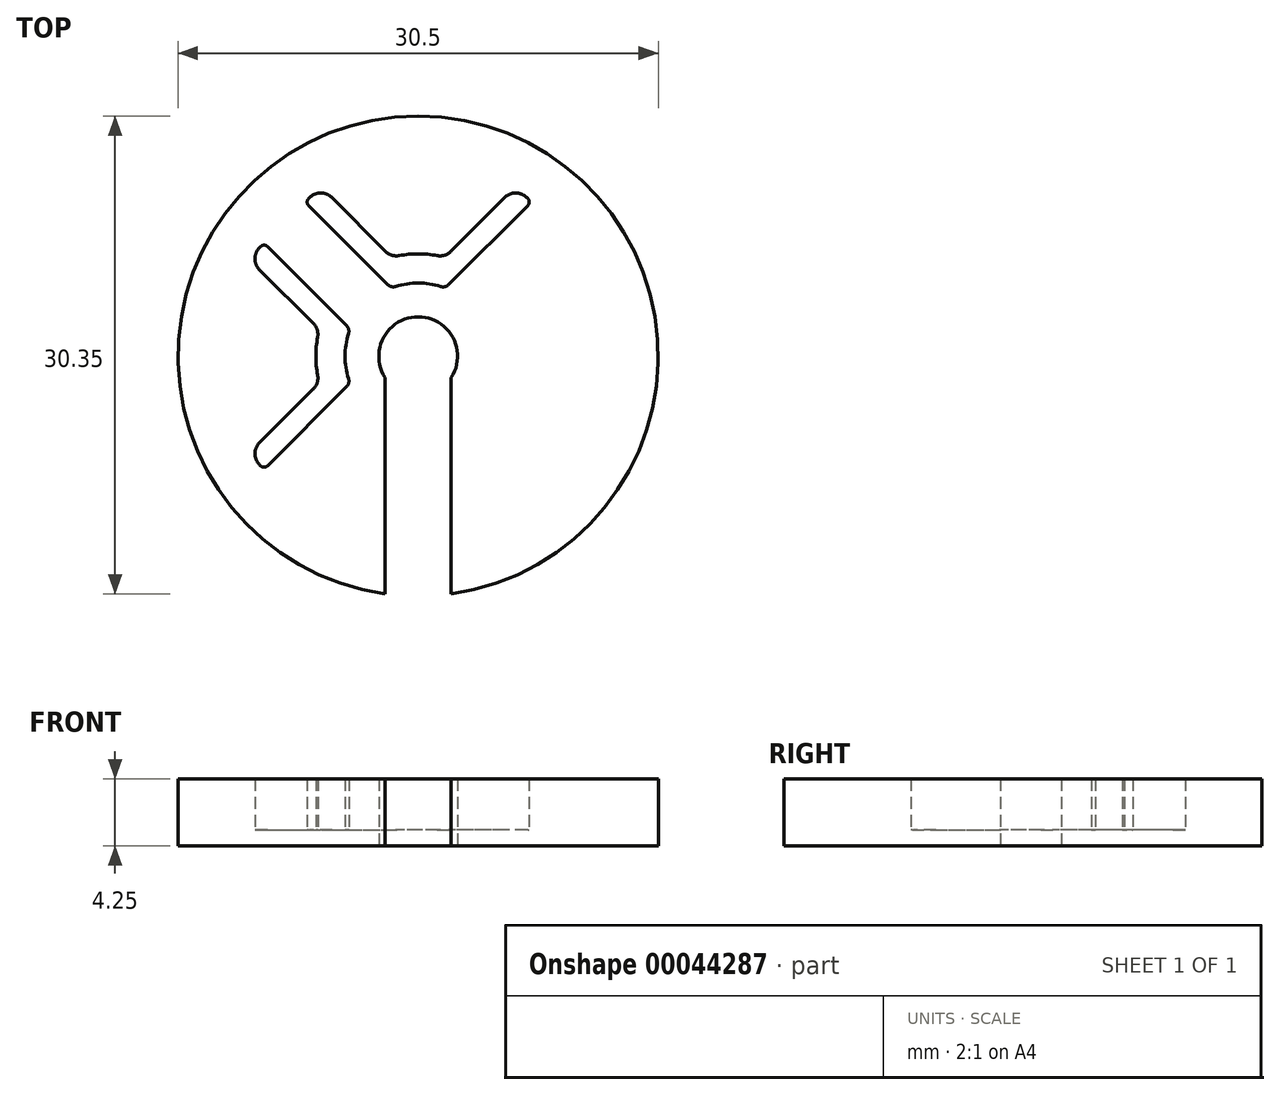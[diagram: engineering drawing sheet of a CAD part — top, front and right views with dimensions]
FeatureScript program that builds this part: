
annotation { "Feature Type Name" : "Feature", "Feature Type Description" : "" }
export const myFeature = defineFeature(function(context is Context, id is Id, definition is map)
    precondition{}
    {
        {
            var Q0;
            Q0=qCreatedBy(makeId("Top.planeOp"),FACE);
            var sketch = newSketch(context, id + "F0", { "sketchPlane" : qUnion([Q0])});
            skCircle(sketch, "E0", {"center": v(0, 0) * mm, "radius": 15.25 * mm});
            skSolve(sketch);
        }
        {
            var Q0;
            Q0 = qSketchRegion(id + "F0", true);
            extrude(context, id + "F1", {"entities" : qUnion([Q0]), "oppositeDirection" : true, "depth" : 1 * mm});
        }
        {
            var Q0;
            Q0=qCreatedBy(makeId("Top.planeOp"),FACE);
            var sketch = newSketch(context, id + "F2", { "sketchPlane" : qUnion([Q0])});
            skLineSegment(sketch, "E1", {"start": v(0, 0) * mm, "end": v(8.49, 8.49) * mm});
            skLineSegment(sketch, "E2", {"start": v(10, 6.97) * mm, "end": v(10.07, 6.9) * mm});
            skArc(sketch, "E3", {"start": v(4.65, 0) * mm, "mid": v(4.6, 0.72) * mm, "end": v(4.43, 1.43) * mm});
            skArc(sketch, "E4.MirrorC", {"start": v(6.39, 1.2) * mm, "mid": v(6.47, 0.6) * mm, "end": v(6.5, 0) * mm});
            skLineSegment(sketch, "E5", {"start": v(9.58, 6.97) * mm, "end": v(4.55, 1.93) * mm});
            skLineSegment(sketch, "E6", {"start": v(10.07, 5.48) * mm, "end": v(6.67, 2.1) * mm});
            skPoint(sketch, "E7.visualSharp", {"position": v(4.32, 1.7) * mm});
            skArc(sketch, "E7.filletArc", {"start": v(4.55, 1.93) * mm, "mid": v(4.42, 1.7) * mm, "end": v(4.43, 1.43) * mm});
            skPoint(sketch, "E8.visualSharp", {"position": v(6.27, 1.7) * mm});
            skArc(sketch, "E8.filletArc", {"start": v(6.67, 2.1) * mm, "mid": v(6.42, 1.69) * mm, "end": v(6.39, 1.2) * mm});
            skPoint(sketch, "E9.visualSharp", {"position": v(9.8, 7.18) * mm});
            skArc(sketch, "E9.filletArc", {"start": v(10, 6.97) * mm, "mid": v(9.8, 7.05) * mm, "end": v(9.58, 6.97) * mm});
            skPoint(sketch, "E10.visualSharp", {"position": v(10.78, 6.19) * mm});
            skArc(sketch, "E10.filletArc", {"start": v(10.07, 5.48) * mm, "mid": v(10.37, 6.19) * mm, "end": v(10.07, 6.9) * mm});
            skArc(sketch, "E11.MirrorCS", {"start": v(1.93, 4.55) * mm, "mid": v(1.7, 4.42) * mm, "end": v(1.43, 4.43) * mm});
            skArc(sketch, "E12.MirrorCS", {"start": v(6.97, 10) * mm, "mid": v(7.05, 9.8) * mm, "end": v(6.97, 9.58) * mm});
            skLineSegment(sketch, "E13.MirrorCS", {"start": v(6.97, 10) * mm, "end": v(6.9, 10.07) * mm});
            skArc(sketch, "E14.MirrorCS", {"start": v(2.1, 6.67) * mm, "mid": v(1.69, 6.42) * mm, "end": v(1.2, 6.39) * mm});
            skArc(sketch, "E15.MirrorCS", {"start": v(5.48, 10.07) * mm, "mid": v(6.19, 10.37) * mm, "end": v(6.9, 10.07) * mm});
            skLineSegment(sketch, "E16.MirrorCS", {"start": v(5.48, 10.07) * mm, "end": v(2.1, 6.67) * mm});
            skPoint(sketch, "E17.MirrorP", {"position": v(7.18, 9.8) * mm});
            skPoint(sketch, "E18.MirrorP", {"position": v(1.7, 4.32) * mm});
            skPoint(sketch, "E19.MirrorP", {"position": v(6.19, 10.78) * mm});
            skLineSegment(sketch, "E20.MirrorCS", {"start": v(6.97, 9.58) * mm, "end": v(1.93, 4.55) * mm});
            skArc(sketch, "E21.MirrorCS", {"start": v(1.2, 6.39) * mm, "mid": v(0.6, 6.47) * mm, "end": v(0, 6.5) * mm});
            skArc(sketch, "E22.MirrorCS", {"start": v(0, 4.65) * mm, "mid": v(0.72, 4.6) * mm, "end": v(1.43, 4.43) * mm});
            skPoint(sketch, "E23.MirrorP", {"position": v(1.7, 6.27) * mm});
            skArc(sketch, "E24.MirrorCS", {"start": v(-6.97, 10) * mm, "mid": v(-7.05, 9.8) * mm, "end": v(-6.97, 9.58) * mm});
            skArc(sketch, "E25.MirrorCS", {"start": v(-10, 6.97) * mm, "mid": v(-9.8, 7.05) * mm, "end": v(-9.58, 6.97) * mm});
            skArc(sketch, "E26.MirrorCS", {"start": v(-1.93, 4.55) * mm, "mid": v(-1.7, 4.42) * mm, "end": v(-1.43, 4.43) * mm});
            skLineSegment(sketch, "E27.MirrorCS", {"start": v(-6.97, 10) * mm, "end": v(-6.9, 10.07) * mm});
            skLineSegment(sketch, "E28.MirrorCS", {"start": v(-10, 6.97) * mm, "end": v(-10.07, 6.9) * mm});
            skArc(sketch, "E29.MirrorCS", {"start": v(-4.55, 1.93) * mm, "mid": v(-4.42, 1.7) * mm, "end": v(-4.43, 1.43) * mm});
            skArc(sketch, "E30.MirrorCS", {"start": v(-6.67, 2.1) * mm, "mid": v(-6.42, 1.69) * mm, "end": v(-6.39, 1.2) * mm});
            skArc(sketch, "E31.MirrorCS", {"start": v(-2.1, 6.67) * mm, "mid": v(-1.69, 6.42) * mm, "end": v(-1.2, 6.39) * mm});
            skArc(sketch, "E32.MirrorCS", {"start": v(-10.07, 5.48) * mm, "mid": v(-10.37, 6.19) * mm, "end": v(-10.07, 6.9) * mm});
            skArc(sketch, "E33.MirrorCS", {"start": v(-6.39, 1.2) * mm, "mid": v(-6.47, 0.6) * mm, "end": v(-6.5, 0) * mm});
            skArc(sketch, "E34.MirrorCS", {"start": v(-4.65, 0) * mm, "mid": v(-4.6, 0.72) * mm, "end": v(-4.43, 1.43) * mm});
            skArc(sketch, "E35.MirrorCS", {"start": v(-1.2, 6.39) * mm, "mid": v(-0.6, 6.47) * mm, "end": v(0, 6.5) * mm});
            skArc(sketch, "E36.MirrorCS", {"start": v(-5.48, 10.07) * mm, "mid": v(-6.19, 10.37) * mm, "end": v(-6.9, 10.07) * mm});
            skLineSegment(sketch, "E37.MirrorCS", {"start": v(-6.97, 9.58) * mm, "end": v(-1.93, 4.55) * mm});
            skLineSegment(sketch, "E38.MirrorCS", {"start": v(-5.48, 10.07) * mm, "end": v(-2.1, 6.67) * mm});
            skPoint(sketch, "E39.MirrorP", {"position": v(-9.8, 7.18) * mm});
            skPoint(sketch, "E40.MirrorP", {"position": v(-1.7, 6.27) * mm});
            skPoint(sketch, "E41.MirrorP", {"position": v(-7.18, 9.8) * mm});
            skArc(sketch, "E42.MirrorCS", {"start": v(0, 4.65) * mm, "mid": v(-0.72, 4.6) * mm, "end": v(-1.43, 4.43) * mm});
            skPoint(sketch, "E43.MirrorP", {"position": v(-6.27, 1.7) * mm});
            skPoint(sketch, "E44.MirrorP", {"position": v(-1.7, 4.32) * mm});
            skPoint(sketch, "E45.MirrorP", {"position": v(-10.78, 6.19) * mm});
            skLineSegment(sketch, "E46.MirrorCS", {"start": v(0, 0) * mm, "end": v(-8.49, 8.49) * mm});
            skPoint(sketch, "E47.MirrorP", {"position": v(-4.32, 1.7) * mm});
            skLineSegment(sketch, "E48.MirrorCS", {"start": v(-10.07, 5.48) * mm, "end": v(-6.67, 2.1) * mm});
            skPoint(sketch, "E49.MirrorP", {"position": v(-6.19, 10.78) * mm});
            skLineSegment(sketch, "E50.MirrorCS", {"start": v(-9.58, 6.97) * mm, "end": v(-4.55, 1.93) * mm});
            skLineSegment(sketch, "E51.MirrorCS", {"start": v(-6.97, -10) * mm, "end": v(-6.9, -10.07) * mm});
            skLineSegment(sketch, "E52.MirrorCS", {"start": v(6.97, -10) * mm, "end": v(6.9, -10.07) * mm});
            skArc(sketch, "E53.MirrorCS", {"start": v(6.97, -10) * mm, "mid": v(7.05, -9.8) * mm, "end": v(6.97, -9.58) * mm});
            skArc(sketch, "E54.MirrorCS", {"start": v(1.93, -4.55) * mm, "mid": v(1.7, -4.42) * mm, "end": v(1.43, -4.43) * mm});
            skArc(sketch, "E55.MirrorCS", {"start": v(10, -6.97) * mm, "mid": v(9.8, -7.05) * mm, "end": v(9.58, -6.97) * mm});
            skArc(sketch, "E56.MirrorCS", {"start": v(4.55, -1.93) * mm, "mid": v(4.42, -1.7) * mm, "end": v(4.43, -1.43) * mm});
            skArc(sketch, "E57.MirrorCS", {"start": v(-4.55, -1.93) * mm, "mid": v(-4.42, -1.7) * mm, "end": v(-4.43, -1.43) * mm});
            skArc(sketch, "E58.MirrorCS", {"start": v(-10, -6.97) * mm, "mid": v(-9.8, -7.05) * mm, "end": v(-9.58, -6.97) * mm});
            skArc(sketch, "E59.MirrorCS", {"start": v(-6.97, -10) * mm, "mid": v(-7.05, -9.8) * mm, "end": v(-6.97, -9.58) * mm});
            skLineSegment(sketch, "E60.MirrorCS", {"start": v(-10, -6.97) * mm, "end": v(-10.07, -6.9) * mm});
            skLineSegment(sketch, "E61.MirrorCS", {"start": v(10, -6.97) * mm, "end": v(10.07, -6.9) * mm});
            skArc(sketch, "E62.MirrorCS", {"start": v(-1.93, -4.55) * mm, "mid": v(-1.7, -4.42) * mm, "end": v(-1.43, -4.43) * mm});
            skArc(sketch, "E63.MirrorCS", {"start": v(-6.67, -2.1) * mm, "mid": v(-6.42, -1.69) * mm, "end": v(-6.39, -1.2) * mm});
            skArc(sketch, "E64.MirrorCS", {"start": v(6.67, -2.1) * mm, "mid": v(6.42, -1.69) * mm, "end": v(6.39, -1.2) * mm});
            skArc(sketch, "E65.MirrorCS", {"start": v(2.1, -6.67) * mm, "mid": v(1.69, -6.42) * mm, "end": v(1.2, -6.39) * mm});
            skArc(sketch, "E66.MirrorCS", {"start": v(-2.1, -6.67) * mm, "mid": v(-1.69, -6.42) * mm, "end": v(-1.2, -6.39) * mm});
            skArc(sketch, "E67.MirrorCS", {"start": v(-1.2, -6.39) * mm, "mid": v(-0.6, -6.47) * mm, "end": v(0, -6.5) * mm});
            skArc(sketch, "E68.MirrorCS", {"start": v(-5.48, -10.07) * mm, "mid": v(-6.19, -10.37) * mm, "end": v(-6.9, -10.07) * mm});
            skArc(sketch, "E69.MirrorCS", {"start": v(10.07, -5.48) * mm, "mid": v(10.37, -6.19) * mm, "end": v(10.07, -6.9) * mm});
            skArc(sketch, "E70.MirrorCS", {"start": v(5.48, -10.07) * mm, "mid": v(6.19, -10.37) * mm, "end": v(6.9, -10.07) * mm});
            skArc(sketch, "E71.MirrorCS", {"start": v(4.65, 0) * mm, "mid": v(4.6, -0.72) * mm, "end": v(4.43, -1.43) * mm});
            skArc(sketch, "E72.MirrorCS", {"start": v(-10.07, -5.48) * mm, "mid": v(-10.37, -6.19) * mm, "end": v(-10.07, -6.9) * mm});
            skArc(sketch, "E73.MirrorCS", {"start": v(-4.65, 0) * mm, "mid": v(-4.6, -0.72) * mm, "end": v(-4.43, -1.43) * mm});
            skLineSegment(sketch, "E74.MirrorCS", {"start": v(6.97, -9.58) * mm, "end": v(1.93, -4.55) * mm});
            skPoint(sketch, "E75.MirrorP", {"position": v(-6.19, -10.78) * mm});
            skLineSegment(sketch, "E76.MirrorCS", {"start": v(-10.07, -5.48) * mm, "end": v(-6.67, -2.1) * mm});
            skArc(sketch, "E77.MirrorCS", {"start": v(0, -4.65) * mm, "mid": v(0.72, -4.6) * mm, "end": v(1.43, -4.43) * mm});
            skArc(sketch, "E78.MirrorCS", {"start": v(0, -4.65) * mm, "mid": v(-0.72, -4.6) * mm, "end": v(-1.43, -4.43) * mm});
            skPoint(sketch, "E79.MirrorP", {"position": v(-1.7, -4.32) * mm});
            skLineSegment(sketch, "E80.MirrorCS", {"start": v(10.07, -5.48) * mm, "end": v(6.67, -2.1) * mm});
            skPoint(sketch, "E81.MirrorP", {"position": v(7.18, -9.8) * mm});
            skLineSegment(sketch, "E82.MirrorCS", {"start": v(9.58, -6.97) * mm, "end": v(4.55, -1.93) * mm});
            skArc(sketch, "E83.MirrorCS", {"start": v(-6.39, -1.2) * mm, "mid": v(-6.47, -0.6) * mm, "end": v(-6.5, 0) * mm});
            skPoint(sketch, "E84.MirrorP", {"position": v(-10.78, -6.19) * mm});
            skPoint(sketch, "E85.MirrorP", {"position": v(1.7, -6.27) * mm});
            skPoint(sketch, "E86.MirrorP", {"position": v(-4.32, -1.7) * mm});
            skArc(sketch, "E87.MirrorCS", {"start": v(6.39, -1.2) * mm, "mid": v(6.47, -0.6) * mm, "end": v(6.5, 0) * mm});
            skLineSegment(sketch, "E88.MirrorCS", {"start": v(-6.97, -9.58) * mm, "end": v(-1.93, -4.55) * mm});
            skPoint(sketch, "E89.MirrorP", {"position": v(1.7, -4.32) * mm});
            skPoint(sketch, "E90.MirrorP", {"position": v(-9.8, -7.18) * mm});
            skLineSegment(sketch, "E91.MirrorCS", {"start": v(5.48, -10.07) * mm, "end": v(2.1, -6.67) * mm});
            skPoint(sketch, "E92.MirrorP", {"position": v(4.32, -1.7) * mm});
            skPoint(sketch, "E93.MirrorP", {"position": v(10.78, -6.19) * mm});
            skPoint(sketch, "E94.MirrorP", {"position": v(-6.27, -1.7) * mm});
            skArc(sketch, "E95.MirrorCS", {"start": v(1.2, -6.39) * mm, "mid": v(0.6, -6.47) * mm, "end": v(0, -6.5) * mm});
            skPoint(sketch, "E96.MirrorP", {"position": v(-7.18, -9.8) * mm});
            skPoint(sketch, "E97.MirrorP", {"position": v(6.27, -1.7) * mm});
            skLineSegment(sketch, "E98.MirrorCS", {"start": v(-5.48, -10.07) * mm, "end": v(-2.1, -6.67) * mm});
            skLineSegment(sketch, "E99.MirrorCS", {"start": v(0, 0) * mm, "end": v(-8.49, -8.49) * mm});
            skLineSegment(sketch, "E100.MirrorCS", {"start": v(-9.58, -6.97) * mm, "end": v(-4.55, -1.93) * mm});
            skLineSegment(sketch, "E101.MirrorCS", {"start": v(0, 0) * mm, "end": v(8.49, -8.49) * mm});
            skPoint(sketch, "E102.MirrorP", {"position": v(6.19, -10.78) * mm});
            skPoint(sketch, "E103.MirrorP", {"position": v(9.8, -7.18) * mm});
            skPoint(sketch, "E104.MirrorP", {"position": v(-1.7, -6.27) * mm});
            skCircle(sketch, "E105", {"center": v(0, 0) * mm, "radius": 15.25 * mm});
            skCircle(sketch, "E106", {"center": v(0, 0) * mm, "radius": 14.6 * mm});
            skSolve(sketch);
        }
        {
            var Q0;
            Q0 = qSketchRegion(id + "F2", true);
            var Q1;
            Q1=makeQuery(id+"F2.imprint","IMPRINT",FACE,{"disambiguationData":[TD([[makeQuery(id+"F2.imprint","IMPRINT",EDGE,{"derivedFrom":sQuery(id+"F2.wireOp",EDGE,"E11.MirrorCS")}),-1.0]])]});
            var Q2;
            Q2=makeQuery(id+"F2.imprint","IMPRINT",FACE,{"disambiguationData":[TD([[makeQuery(id+"F2.imprint","IMPRINT",EDGE,{"derivedFrom":sQuery(id+"F2.wireOp",EDGE,"E2")}),-1.0]])]});
            var Q3;
            Q3=makeQuery(id+"F2.imprint","IMPRINT",FACE,{"disambiguationData":[TD([[makeQuery(id+"F2.imprint","IMPRINT",EDGE,{"derivedFrom":sQuery(id+"F2.wireOp",EDGE,"E25.MirrorCS")}),-1.0]])]});
            var Q4;
            Q4=makeQuery(id+"F2.imprint","IMPRINT",FACE,{"disambiguationData":[TD([[makeQuery(id+"F2.imprint","IMPRINT",EDGE,{"derivedFrom":sQuery(id+"F2.wireOp",EDGE,"E51.MirrorCS")}),1.0]])]});
            extrude(context, id + "F3", {"entities" : qUnion([Q0, Q1, Q2, Q3, Q4]), "operationType" : NewBodyOperationType.ADD, "depth" : 3.25 * mm});
        }
        {
            var Q0;
            Q0=makeQuery(id+"F1.opExtrude","CAP_FACE",FACE,{"disambiguationData":[OSD([sQuery(id+"F0.wireOp",EDGE,"E0")])],"isStart":false});
            var sketch = newSketch(context, id + "F4", { "sketchPlane" : qUnion([Q0])});
            skLineSegment(sketch, "E107", {"start": v(0, 0) * mm, "end": v(2.1, 0) * mm});
            skLineSegment(sketch, "E108", {"start": v(0, 0) * mm, "end": v(0, 16) * mm});
            skArc(sketch, "E109", {"start": v(-2.1, 1.36) * mm, "mid": v(0, -2.5) * mm, "end": v(2.1, 1.36) * mm});
            skLineSegment(sketch, "E110.bottom", {"start": v(0, 16) * mm, "end": v(2.1, 16) * mm});
            skLineSegment(sketch, "E110.left", {"start": v(0, 16) * mm, "end": v(0, 0) * mm});
            skLineSegment(sketch, "E110.right", {"start": v(2.1, 16) * mm, "end": v(2.1, 1.36) * mm});
            skLineSegment(sketch, "E111.MirrorCS", {"start": v(0, 0) * mm, "end": v(-2.1, 0) * mm});
            skLineSegment(sketch, "E112.MirrorCS", {"start": v(-2.1, 16) * mm, "end": v(-2.1, 1.36) * mm});
            skLineSegment(sketch, "E113.MirrorCS", {"start": v(0, 16) * mm, "end": v(-2.1, 16) * mm});
            skArc(sketch, "E114.MirrorC", {"start": v(2.1, 1.36) * mm, "mid": v(0, -2.5) * mm, "end": v(-2.1, 1.36) * mm});
            skSolve(sketch);
        }
        {
            var Q0;
            Q0 = qSketchRegion(id + "F4", true);
            extrude(context, id + "F5", {"entities" : qUnion([Q0]), "operationType" : NewBodyOperationType.REMOVE, "endBound" : BoundingType.THROUGH_ALL, "oppositeDirection" : true, "depth" : 25 * mm});
        }
    });
